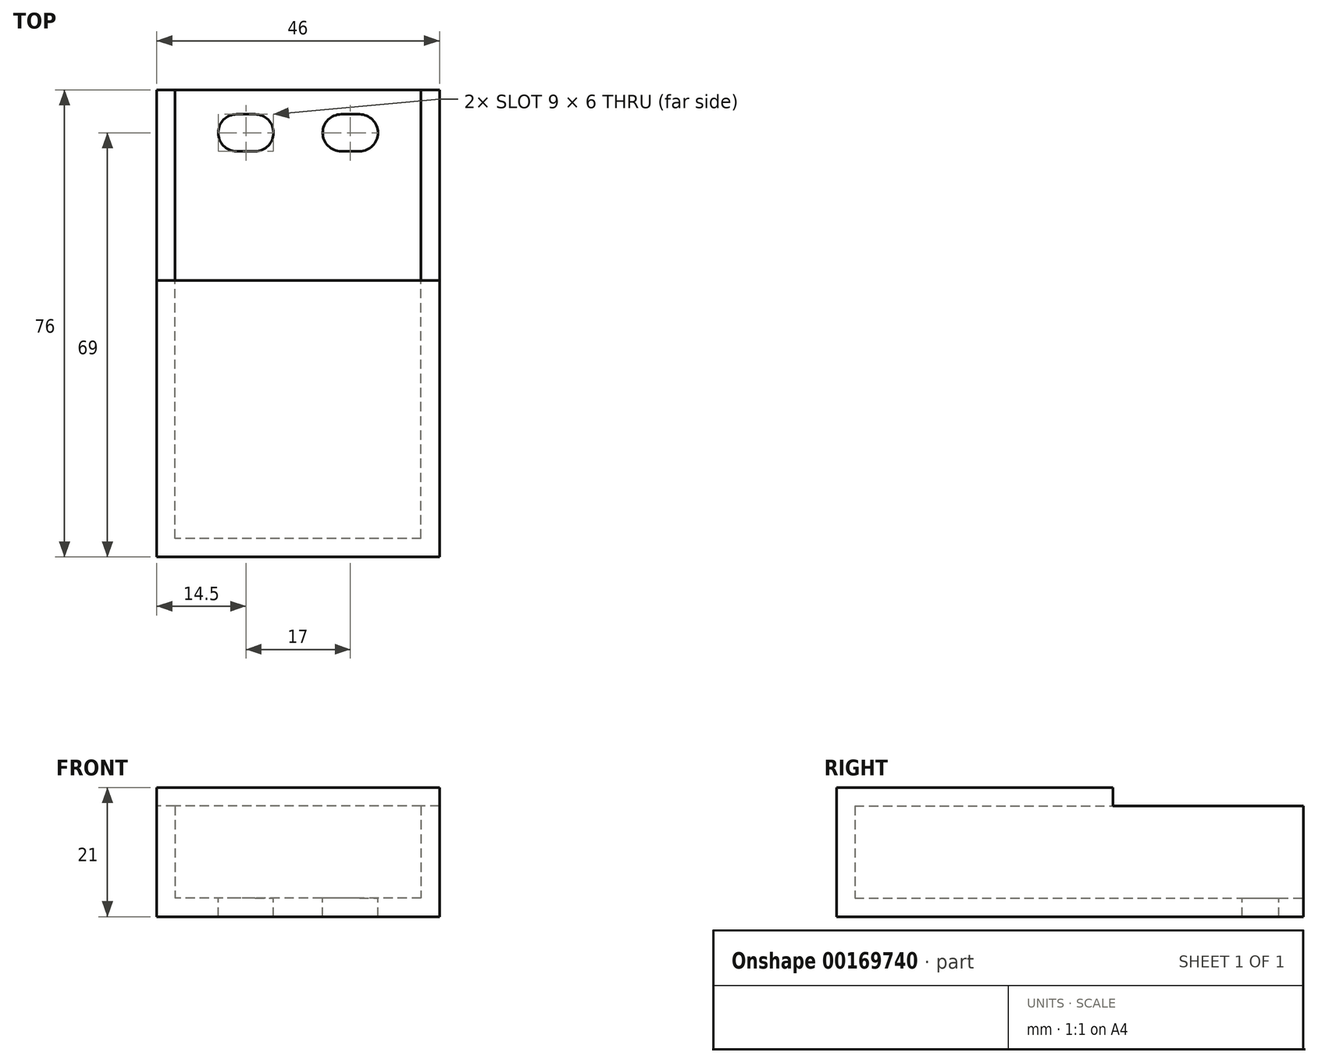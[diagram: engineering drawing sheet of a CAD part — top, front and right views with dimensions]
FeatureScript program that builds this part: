
annotation { "Feature Type Name" : "Feature", "Feature Type Description" : "" }
export const myFeature = defineFeature(function(context is Context, id is Id, definition is map)
    precondition{}
    {
        {
            var Q0;
            Q0=qCreatedBy(makeId("Top.planeOp"),FACE);
            var sketch = newSketch(context, id + "F0", { "sketchPlane" : qUnion([Q0])});
            skLineSegment(sketch, "E0.bottom", {"start": v(23, -38) * mm, "end": v(-23, -38) * mm});
            skLineSegment(sketch, "E0.top", {"start": v(23, 38) * mm, "end": v(-23, 38) * mm});
            skLineSegment(sketch, "E0.left", {"start": v(23, -38) * mm, "end": v(23, 38) * mm});
            skLineSegment(sketch, "E0.right", {"start": v(-23, -38) * mm, "end": v(-23, 38) * mm});
            skPoint(sketch, "E0.middle", {"position": v(0, 0) * mm});
            skSolve(sketch);
        }
        {
            var Q0;
            Q0=makeQuery(id+"F0.imprint","IMPRINT",FACE,{"disambiguationData":[TD([[makeQuery(id+"F0.imprint","IMPRINT",EDGE,{"derivedFrom":sQuery(id+"F0.wireOp",EDGE,"E0.bottom")}),-1.0]])]});
            extrude(context, id + "F1", {"entities" : qUnion([Q0]), "depth" : 3 * mm});
        }
        {
            var Q0;
            Q0=makeQuery(id+"F1.opExtrude","CAP_FACE",FACE,{"disambiguationData":[OSD([sQuery(id+"F0.wireOp",EDGE,"E0.bottom"),sQuery(id+"F0.wireOp",EDGE,"E0.top"),sQuery(id+"F0.wireOp",EDGE,"E0.left"),sQuery(id+"F0.wireOp",EDGE,"E0.right")])],"isStart":false});
            var sketch = newSketch(context, id + "F2", { "sketchPlane" : qUnion([Q0])});
            skLineSegment(sketch, "E1.bottom", {"start": v(20, -35) * mm, "end": v(-20, -35) * mm});
            skLineSegment(sketch, "E1.top", {"start": v(20, 35) * mm, "end": v(-20, 35) * mm});
            skLineSegment(sketch, "E1.left", {"start": v(20, -35) * mm, "end": v(20, 35) * mm});
            skLineSegment(sketch, "E1.right", {"start": v(-20, -35) * mm, "end": v(-20, 35) * mm});
            skPoint(sketch, "E1.middle", {"position": v(0, 0) * mm});
            skLineSegment(sketch, "E2.bottom", {"start": v(23, 38) * mm, "end": v(-23, 38) * mm});
            skLineSegment(sketch, "E2.top", {"start": v(23, -38) * mm, "end": v(-23, -38) * mm});
            skLineSegment(sketch, "E2.left", {"start": v(23, 38) * mm, "end": v(23, -38) * mm});
            skLineSegment(sketch, "E2.right", {"start": v(-23, 38) * mm, "end": v(-23, -38) * mm});
            skSolve(sketch);
        }
        {
            var Q0;
            Q0=makeQuery(id+"F2.imprint","IMPRINT",FACE,{"disambiguationData":[TD([[makeQuery(id+"F2.imprint","IMPRINT",EDGE,{"derivedFrom":sQuery(id+"F2.wireOp",EDGE,"E1.bottom")}),1.0]])]});
            extrude(context, id + "F3", {"entities" : qUnion([Q0]), "operationType" : NewBodyOperationType.ADD, "depth" : 15 * mm});
        }
        {
            var Q0;
            Q0=makeQuery(id+"FKHxS5iHxNJSU2c_1.boolean.opBoolean","MERGE",FACE,{"derivedFrom":[makeQuery(id+"F1.opExtrude","CAP_FACE",FACE,{"disambiguationData":[OSD([sQuery(id+"F0.wireOp",EDGE,"E0.bottom"),sQuery(id+"F0.wireOp",EDGE,"E0.top"),sQuery(id+"F0.wireOp",EDGE,"E0.left"),sQuery(id+"F0.wireOp",EDGE,"E0.right")])],"isStart":false}),makeQuery(id+"FKHxS5iHxNJSU2c_1.opExtrude","SWEPT_FACE",FACE,{"disambiguationData":[OSD([sQuery(id+"Fw28Vis8vk2JBkK_1.wireOp",EDGE,"Iw1cpI2y-pTmP-6fhk-ulBS-wUrXH71GQpCD.top")])]})]});
            var sketch = newSketch(context, id + "F4", { "sketchPlane" : qUnion([Q0])});
            skArc(sketch, "E3", {"start": v(-7, 28) * mm, "mid": v(-4, 31) * mm, "end": v(-7, 34) * mm});
            skArc(sketch, "E4", {"start": v(7, 34) * mm, "mid": v(4, 31) * mm, "end": v(7, 28) * mm});
            skLineSegment(sketch, "E5", {"start": v(-7, 31) * mm, "end": v(7, 31) * mm, "construction": true});
            skPoint(sketch, "E6", {"position": v(0, -35) * mm});
            skPoint(sketch, "E7", {"position": v(0, 31) * mm});
            skArc(sketch, "E8", {"start": v(-10, 34) * mm, "mid": v(-13, 31) * mm, "end": v(-10, 28) * mm});
            skLineSegment(sketch, "E9", {"start": v(-7, 34) * mm, "end": v(-10, 34) * mm});
            skLineSegment(sketch, "E10", {"start": v(-7, 28) * mm, "end": v(-10, 28) * mm});
            skArc(sketch, "E11", {"start": v(10, 28) * mm, "mid": v(13, 31) * mm, "end": v(10, 34) * mm});
            skLineSegment(sketch, "E12", {"start": v(10, 34) * mm, "end": v(7, 34) * mm});
            skLineSegment(sketch, "E13", {"start": v(10, 28) * mm, "end": v(7, 28) * mm});
            skSolve(sketch);
        }
        {
            var Q0;
            Q0=makeQuery(id+"F4.imprint","IMPRINT",FACE,{"disambiguationData":[TD([[makeQuery(id+"F4.imprint","IMPRINT",EDGE,{"derivedFrom":sQuery(id+"F4.wireOp",EDGE,"E3")}),1.0]])]});
            var Q1;
            Q1=makeQuery(id+"F4.imprint","IMPRINT",FACE,{"disambiguationData":[TD([[makeQuery(id+"F4.imprint","IMPRINT",EDGE,{"derivedFrom":sQuery(id+"F4.wireOp",EDGE,"E4")}),1.0]])]});
            extrude(context, id + "F5", {"entities" : qUnion([Q0, Q1]), "operationType" : NewBodyOperationType.REMOVE, "oppositeDirection" : true, "depth" : 25 * mm});
        }
        {
            var Q0;
            Q0=makeQuery(id+"F3.opExtrude","CAP_FACE",FACE,{"disambiguationData":[OSD([sQuery(id+"F2.wireOp",EDGE,"E1.bottom"),sQuery(id+"F2.wireOp",EDGE,"E1.top"),sQuery(id+"F2.wireOp",EDGE,"E1.left"),sQuery(id+"F2.wireOp",EDGE,"E1.right"),sQuery(id+"F2.wireOp",EDGE,"E2.bottom"),sQuery(id+"F2.wireOp",EDGE,"E2.top"),sQuery(id+"F2.wireOp",EDGE,"E2.left"),sQuery(id+"F2.wireOp",EDGE,"E2.right")])],"isStart":false});
            var sketch = newSketch(context, id + "F6", { "sketchPlane" : qUnion([Q0])});
            skLineSegment(sketch, "E14.bottom", {"start": v(-23, -38) * mm, "end": v(23, -38) * mm});
            skLineSegment(sketch, "E14.top", {"start": v(-23, 7) * mm, "end": v(23, 7) * mm});
            skLineSegment(sketch, "E14.left", {"start": v(-23, -38) * mm, "end": v(-23, 7) * mm});
            skLineSegment(sketch, "E14.right", {"start": v(23, -38) * mm, "end": v(23, 7) * mm});
            skSolve(sketch);
        }
        {
            var Q0;
            Q0=makeQuery(id+"F6.imprint","IMPRINT",FACE,{"disambiguationData":[TD([[makeQuery(id+"F6.imprint","IMPRINT",EDGE,{"derivedFrom":sQuery(id+"F6.wireOp",EDGE,"E14.bottom")}),-1.0]])]});
            var Q1;
            {var subQ5=makeQuery(id+"F3.opExtrude","CAP_EDGE",EDGE,{"disambiguationData":[OSD([sQuery(id+"F2.wireOp",EDGE,"E1.bottom")])],"isStart":false});Q1=makeQuery(id+"F6.imprint","IMPRINT",FACE,{"disambiguationData":[TD([[makeQuery(id+"F6.imprint","IMPRINT",EDGE,{"derivedFrom":subQ5}),-1.0]])]});}
            extrude(context, id + "F7", {"entities" : qUnion([Q0, Q1]), "operationType" : NewBodyOperationType.ADD, "depth" : 3 * mm});
        }
        {
            var Q0;
            Q0=makeQuery(id+"F3.opExtrude","SWEPT_FACE",FACE,{"disambiguationData":[OSD([sQuery(id+"F2.wireOp",EDGE,"E1.top")])]});
            extrude(context, id + "F8", {"entities" : qUnion([Q0]), "operationType" : NewBodyOperationType.REMOVE, "oppositeDirection" : true, "depth" : 25 * mm});
        }
    });
